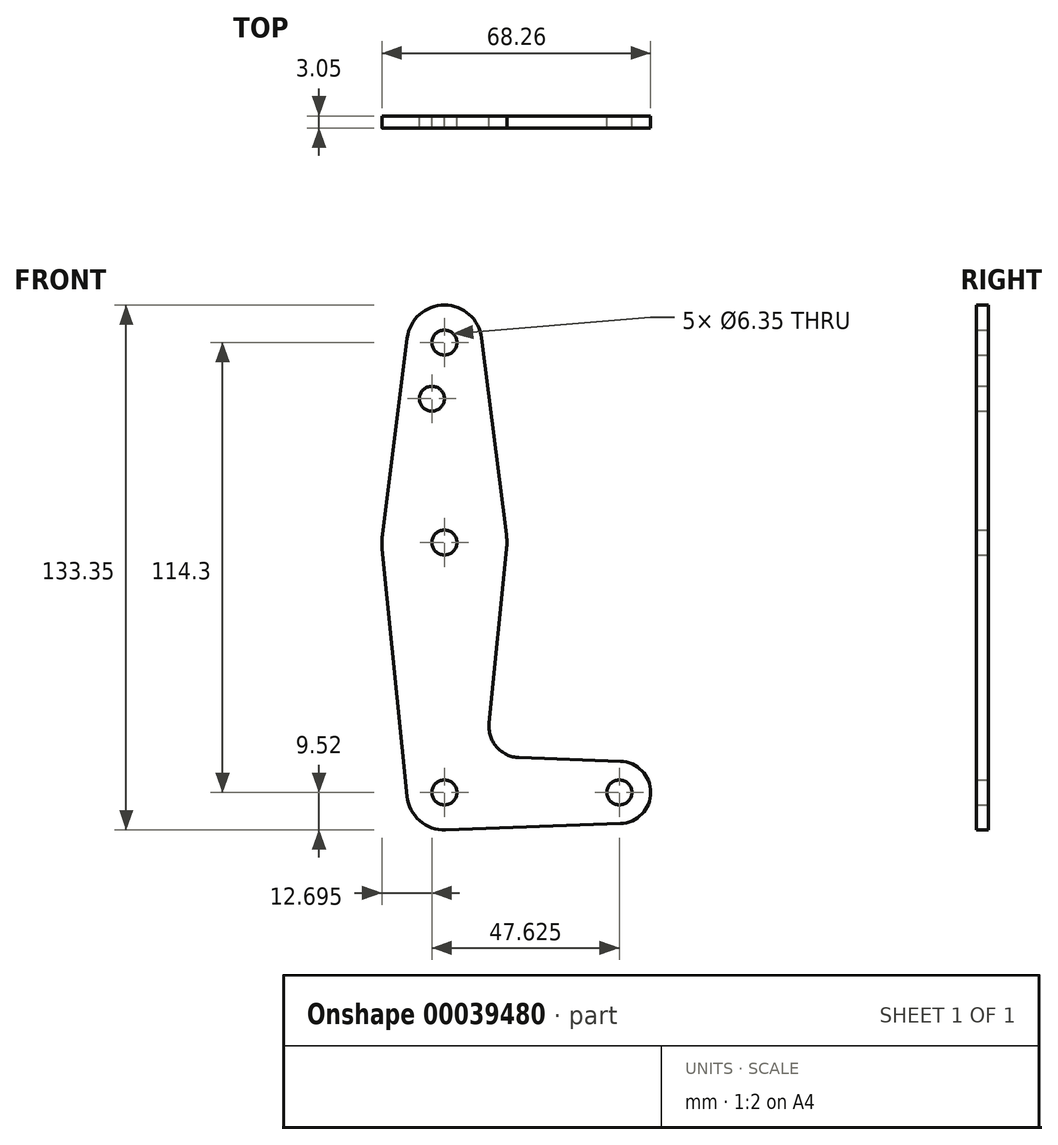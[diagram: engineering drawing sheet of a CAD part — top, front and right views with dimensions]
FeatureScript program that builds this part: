
annotation { "Feature Type Name" : "Feature", "Feature Type Description" : "" }
export const myFeature = defineFeature(function(context is Context, id is Id, definition is map)
    precondition{}
    {
        {
            var Q0;
            Q0=qCreatedBy(makeId("Front.planeOp"),FACE);
            var sketch = newSketch(context, id + "F0", { "sketchPlane" : qUnion([Q0])});
            skLineSegment(sketch, "E0", {"start": v(0, 0) * mm, "end": v(0, 114.3) * mm, "construction": true});
            skLineSegment(sketch, "E1", {"start": v(0, 0) * mm, "end": v(44.45, 0) * mm, "construction": true});
            skCircle(sketch, "E2", {"center": v(0, 114.3) * mm, "radius": 9.53 * mm});
            skCircle(sketch, "E3", {"center": v(0, 0) * mm, "radius": 9.53 * mm});
            skCircle(sketch, "E4", {"center": v(44.45, 0) * mm, "radius": 7.94 * mm});
            skCircle(sketch, "E5", {"center": v(0, 63.5) * mm, "radius": 15.88 * mm});
            skLineSegment(sketch, "E6", {"start": v(-9.45, 115.5) * mm, "end": v(-15.75, 65.48) * mm});
            skLineSegment(sketch, "E7", {"start": v(9.45, 115.5) * mm, "end": v(15.75, 65.48) * mm});
            skLineSegment(sketch, "E8", {"start": v(-9.48, -0.95) * mm, "end": v(-15.8, 61.91) * mm});
            skLineSegment(sketch, "E9", {"start": v(11.34, 17.6) * mm, "end": v(15.8, 61.91) * mm});
            skLineSegment(sketch, "E10", {"start": v(0.34, -9.52) * mm, "end": v(44.73, -7.93) * mm});
            skLineSegment(sketch, "E11", {"start": v(18.97, 8.85) * mm, "end": v(44.73, 7.93) * mm});
            skCircle(sketch, "E12", {"center": v(0, 114.3) * mm, "radius": 3.18 * mm});
            skCircle(sketch, "E13", {"center": v(0, 0) * mm, "radius": 3.18 * mm});
            skCircle(sketch, "E14", {"center": v(44.45, 0) * mm, "radius": 3.18 * mm});
            skCircle(sketch, "E15", {"center": v(0, 63.5) * mm, "radius": 3.18 * mm});
            skCircle(sketch, "E16", {"center": v(-3.18, 100.03) * mm, "radius": 3.18 * mm});
            skArc(sketch, "E17.filletArc", {"start": v(11.34, 17.6) * mm, "mid": v(13.26, 11.57) * mm, "end": v(18.97, 8.85) * mm});
            skSolve(sketch);
        }
        {
            var Q0;
            Q0 = qSketchRegion(id + "F0", true);
            extrude(context, id + "F1", {"entities" : qUnion([Q0]), "depth" : 3.05 * mm});
        }
    });
